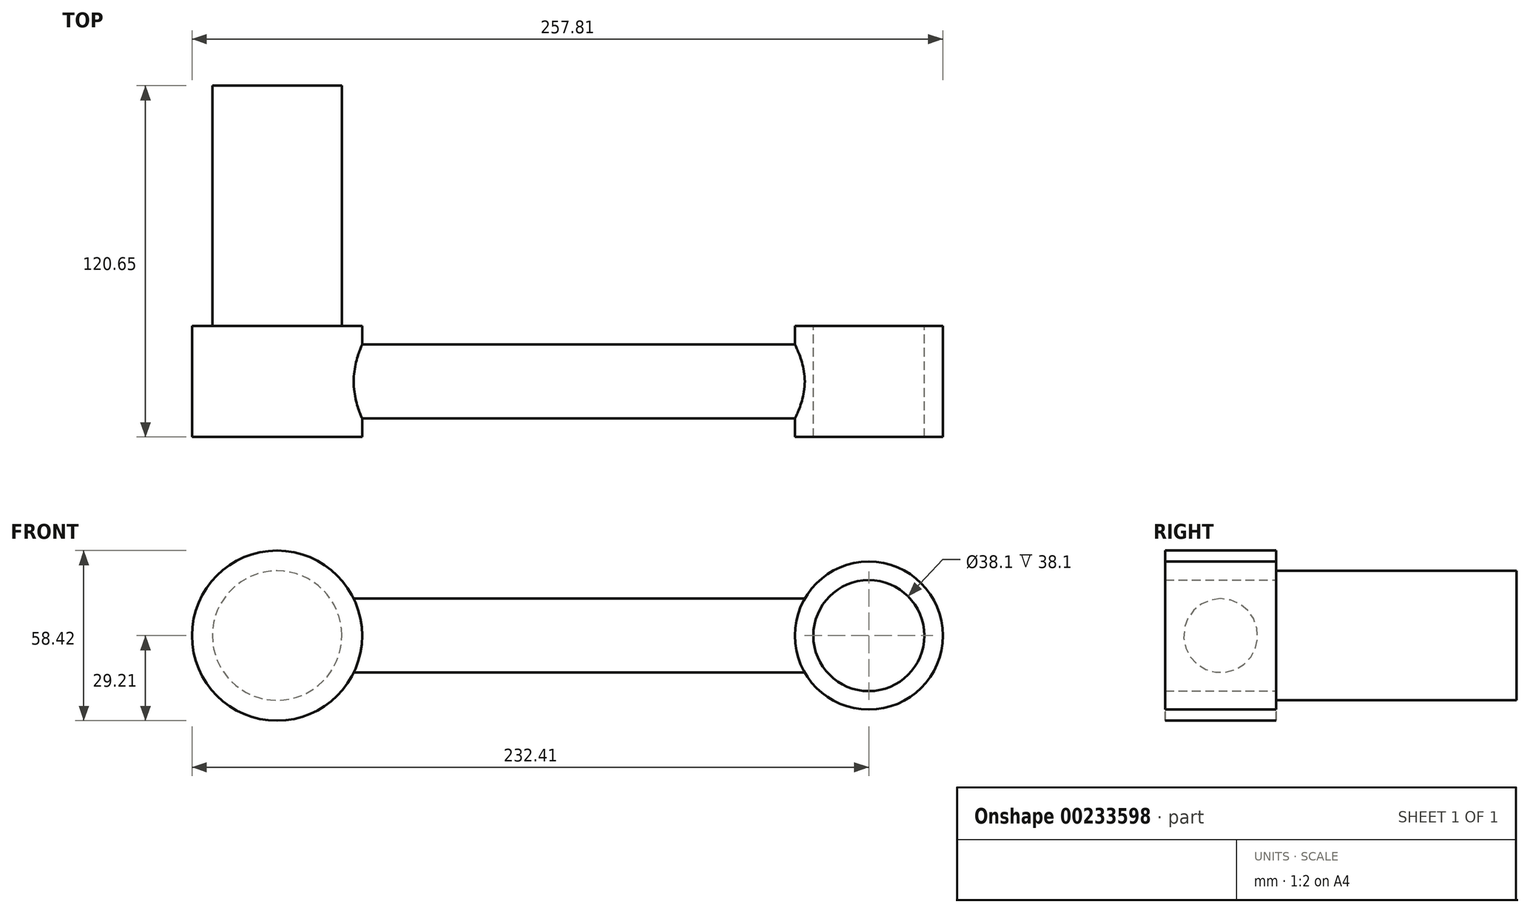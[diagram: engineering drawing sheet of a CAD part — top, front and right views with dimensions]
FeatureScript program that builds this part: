
annotation { "Feature Type Name" : "Feature", "Feature Type Description" : "" }
export const myFeature = defineFeature(function(context is Context, id is Id, definition is map)
    precondition{}
    {
        {
            var Q0;
            Q0=qCreatedBy(makeId("Front.planeOp"),FACE);
            var sketch = newSketch(context, id + "F0", { "sketchPlane" : qUnion([Q0])});
            skLineSegment(sketch, "E0", {"start": v(0, 0) * mm, "end": v(203.2, 0) * mm, "construction": true});
            skCircle(sketch, "E1", {"center": v(0, 0) * mm, "radius": 22.23 * mm});
            skCircle(sketch, "E2", {"center": v(0, 0) * mm, "radius": 29.21 * mm});
            skCircle(sketch, "E3", {"center": v(203.2, 0) * mm, "radius": 19.05 * mm});
            skCircle(sketch, "E4", {"center": v(203.2, 0) * mm, "radius": 25.4 * mm});
            skSolve(sketch);
        }
        {
            var Q0;
            Q0=qCreatedBy(makeId("Right.planeOp"),FACE);
            var sketch = newSketch(context, id + "F1", { "sketchPlane" : qUnion([Q0])});
            skCircle(sketch, "E5", {"center": v(0, 0) * mm, "radius": 12.7 * mm});
            skSolve(sketch);
        }
        {
            var Q0;
            Q0=makeQuery(id+"F0.imprint","IMPRINT",FACE,{"disambiguationData":[TD([[makeQuery(id+"F0.imprint","IMPRINT",EDGE,{"derivedFrom":sQuery(id+"F0.wireOp",EDGE,"E1")}),-1.0]])]});
            var Q1;
            Q1=makeQuery(id+"F0.imprint","IMPRINT",FACE,{"disambiguationData":[TD([[makeQuery(id+"F0.imprint","IMPRINT",EDGE,{"derivedFrom":sQuery(id+"F0.wireOp",EDGE,"E3")}),-1.0]])]});
            extrude(context, id + "F2", {"entities" : qUnion([Q0, Q1]), "endBound" : BoundingType.SYMMETRIC, "depth" : 38.1 * mm});
        }
        {
            var Q0;
            Q0=makeQuery(id+"F1.imprint","IMPRINT",FACE,{"disambiguationData":[TD([[makeQuery(id+"F1.imprint","IMPRINT",EDGE,{"derivedFrom":sQuery(id+"F1.wireOp",EDGE,"E5")}),1.0]])]});
            var Q1;
            Q1=sQuery(id+"F1.wireOp",EDGE,"E5");
            var Q2;
            Q2=makeQuery(id+"F2.opExtrude","SWEPT_FACE",FACE,{"disambiguationData":[OSD([sQuery(id+"F0.wireOp",EDGE,"E4")])]});
            var Q3;
            Q3=makeQuery(id+"F2.opExtrude","SWEPT_FACE",FACE,{"disambiguationData":[OSD([sQuery(id+"F0.wireOp",EDGE,"E2")])]});
            extrude(context, id + "F3", {"entities" : qUnion([Q0]), "operationType" : NewBodyOperationType.ADD, "surfaceEntities" : qUnion([Q1]), "endBound" : BoundingType.UP_TO_SURFACE, "endBoundEntityFace" : qUnion([Q2]), "depth" : 25.4 * mm, "hasSecondDirection" : true, "secondDirectionBound" : SecondDirectionBoundingType.UP_TO_SURFACE, "secondDirectionOppositeDirection" : false, "secondDirectionBoundEntityFace" : qUnion([Q3]), "secondDirectionDepth" : 25.4 * mm});
        }
        {
            var Q0;
            Q0=makeQuery(id+"F0.imprint","IMPRINT",FACE,{"disambiguationData":[TD([[makeQuery(id+"F0.imprint","IMPRINT",EDGE,{"derivedFrom":sQuery(id+"F0.wireOp",EDGE,"E1")}),1.0]])]});
            extrude(context, id + "F4", {"entities" : qUnion([Q0]), "operationType" : NewBodyOperationType.ADD, "depth" : 19.05 * mm, "hasSecondDirection" : true, "secondDirectionOppositeDirection" : true, "secondDirectionDepth" : 101.6 * mm});
        }
    });
